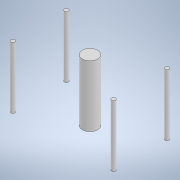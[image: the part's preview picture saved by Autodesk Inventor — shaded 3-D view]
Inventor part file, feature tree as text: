
AUTODESK INVENTOR PART (.ipt)
format: ipt  version: 2022 (Build 260153000, 153)  size: 107,520 bytes
history: native  units: mm
features: extrude x1, sketch x1
ambient origin geometry x8: Origin, YZ Plane, XZ Plane, XY Plane, X Axis, Y Axis, Z Axis, Center Point
bodies: Solid1 (feature_tree)
feature tree (2):
  extrude  "Extrusion1"  Depth=50.0mm
  sketch  "Sketch1"  dims[d0=82.08mm d1=43.55mm d2=3.3mm d3=12.5mm d6=56.4655mm d7=41.04mm d8=50.0mm d9=0.0mm]
